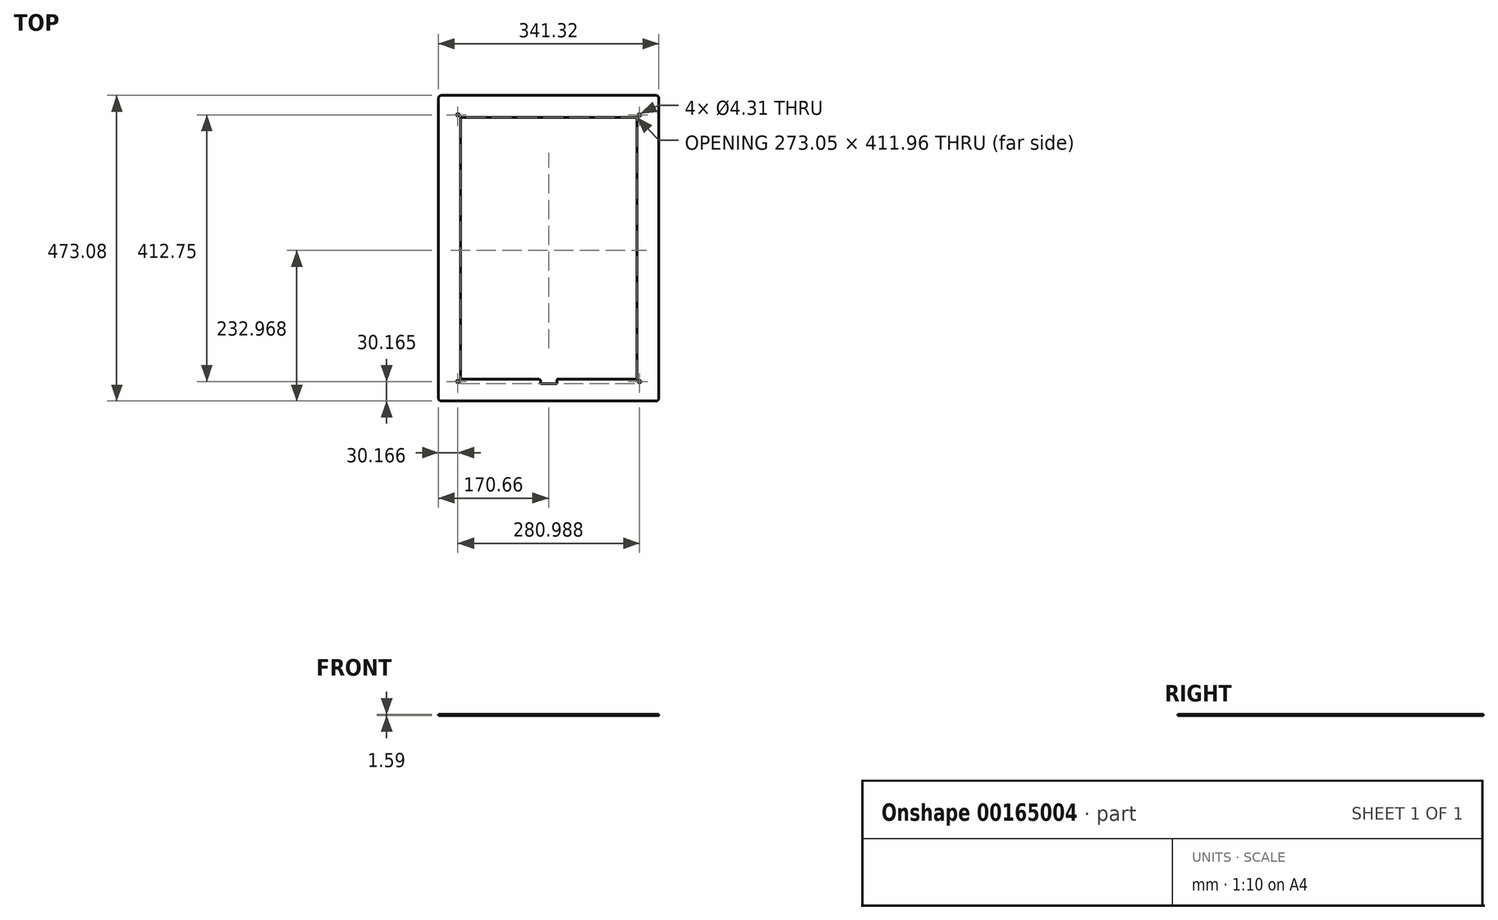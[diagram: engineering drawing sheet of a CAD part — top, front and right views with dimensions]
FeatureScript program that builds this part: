
annotation { "Feature Type Name" : "Feature", "Feature Type Description" : "" }
export const myFeature = defineFeature(function(context is Context, id is Id, definition is map)
    precondition{}
    {
        {
            var Q0;
            Q0=qCreatedBy(makeId("Top.planeOp"),FACE);
            var sketch = newSketch(context, id + "F0", { "sketchPlane" : qUnion([Q0])});
            skLineSegment(sketch, "E0.bottom", {"start": v(170.66, -236.54) * mm, "end": v(-170.66, -236.54) * mm});
            skLineSegment(sketch, "E0.top", {"start": v(170.66, 236.54) * mm, "end": v(-170.66, 236.54) * mm});
            skLineSegment(sketch, "E0.left", {"start": v(170.66, -236.54) * mm, "end": v(170.66, 236.54) * mm});
            skLineSegment(sketch, "E0.right", {"start": v(-170.66, -236.54) * mm, "end": v(-170.66, 236.54) * mm});
            skPoint(sketch, "E0.middle", {"position": v(0, 0) * mm});
            skLineSegment(sketch, "E1.bottom", {"start": v(140.5, 206.38) * mm, "end": v(-140.5, 206.38) * mm, "construction": true});
            skLineSegment(sketch, "E1.top", {"start": v(140.5, -206.38) * mm, "end": v(-140.5, -206.38) * mm, "construction": true});
            skLineSegment(sketch, "E1.left", {"start": v(140.5, 206.38) * mm, "end": v(140.5, -206.38) * mm, "construction": true});
            skLineSegment(sketch, "E1.right", {"start": v(-140.5, 206.38) * mm, "end": v(-140.5, -206.38) * mm, "construction": true});
            skLineSegment(sketch, "E2.bottom", {"start": v(136.53, 202.4) * mm, "end": v(-136.53, 202.4) * mm});
            skLineSegment(sketch, "E2.top", {"start": v(136.53, -202.4) * mm, "end": v(-136.53, -202.4) * mm});
            skLineSegment(sketch, "E2.left", {"start": v(136.53, 202.4) * mm, "end": v(136.53, -202.4) * mm});
            skLineSegment(sketch, "E2.right", {"start": v(-136.53, 202.4) * mm, "end": v(-136.53, -202.4) * mm});
            skLineSegment(sketch, "E3", {"start": v(136.53, 202.4) * mm, "end": v(136.53, 206.38) * mm, "construction": true});
            skLineSegment(sketch, "E4", {"start": v(136.53, 202.4) * mm, "end": v(140.5, 202.4) * mm, "construction": true});
            skLineSegment(sketch, "E5", {"start": v(140.5, 206.38) * mm, "end": v(140.5, 236.54) * mm, "construction": true});
            skLineSegment(sketch, "E6", {"start": v(140.5, 206.38) * mm, "end": v(170.66, 206.38) * mm, "construction": true});
            skCircle(sketch, "E7", {"center": v(-140.5, 206.38) * mm, "radius": 2.15 * mm});
            skCircle(sketch, "E8", {"center": v(140.5, 206.38) * mm, "radius": 2.15 * mm});
            skCircle(sketch, "E9", {"center": v(140.5, -206.38) * mm, "radius": 2.15 * mm});
            skCircle(sketch, "E10", {"center": v(-140.5, -206.38) * mm, "radius": 2.15 * mm});
            skSolve(sketch);
        }
        {
            var Q0;
            Q0 = qSketchRegion(id + "F0", true);
            extrude(context, id + "F1", {"entities" : qUnion([Q0]), "depth" : 1.59 * mm});
        }
        {
            var Q0;
            Q0=makeQuery(id+"F1.opExtrude","SWEPT_EDGE",EDGE,{"disambiguationData":[OSD([sQuery(id+"F0.wireOp",EDGE,"E0.top"),sQuery(id+"F0.wireOp",EDGE,"E0.right")])]});
            var Q1;
            Q1=makeQuery(id+"F1.opExtrude","SWEPT_EDGE",EDGE,{"disambiguationData":[OSD([sQuery(id+"F0.wireOp",EDGE,"E0.top"),sQuery(id+"F0.wireOp",EDGE,"E0.left")])]});
            var Q2;
            Q2=makeQuery(id+"F1.opExtrude","SWEPT_EDGE",EDGE,{"disambiguationData":[OSD([sQuery(id+"F0.wireOp",EDGE,"E0.bottom"),sQuery(id+"F0.wireOp",EDGE,"E0.left")])]});
            var Q3;
            Q3=makeQuery(id+"F1.opExtrude","SWEPT_EDGE",EDGE,{"disambiguationData":[OSD([sQuery(id+"F0.wireOp",EDGE,"E0.bottom"),sQuery(id+"F0.wireOp",EDGE,"E0.right")])]});
            fillet(context, id + "F2", {"entities" : qUnion([Q0, Q1, Q2, Q3]), "radius" : 4.76 * mm, "tangentPropagation" : true, "allowEdgeOverflow" : false});
        }
        {
            var Q0;
            Q0=makeQuery(id+"F1.opExtrude","CAP_FACE",FACE,{"disambiguationData":[OSD([sQuery(id+"F0.wireOp",EDGE,"E0.bottom"),sQuery(id+"F0.wireOp",EDGE,"E0.top"),sQuery(id+"F0.wireOp",EDGE,"E0.left"),sQuery(id+"F0.wireOp",EDGE,"E0.right"),sQuery(id+"F0.wireOp",EDGE,"E2.bottom"),sQuery(id+"F0.wireOp",EDGE,"E2.top"),sQuery(id+"F0.wireOp",EDGE,"E2.left"),sQuery(id+"F0.wireOp",EDGE,"E2.right"),sQuery(id+"F0.wireOp",EDGE,"E7"),sQuery(id+"F0.wireOp",EDGE,"E8"),sQuery(id+"F0.wireOp",EDGE,"E9"),sQuery(id+"F0.wireOp",EDGE,"E10")])],"isStart":false});
            var sketch = newSketch(context, id + "F3", { "sketchPlane" : qUnion([Q0])});
            skLineSegment(sketch, "E11", {"start": v(-140.5, -206.38) * mm, "end": v(-140.5, -211.14) * mm, "construction": true});
            skLineSegment(sketch, "E12", {"start": v(-140.5, -211.14) * mm, "end": v(0, -211.14) * mm, "construction": true});
            skLineSegment(sketch, "E13", {"start": v(0, -211.14) * mm, "end": v(0, -209.55) * mm, "construction": true});
            skLineSegment(sketch, "E14.bottom", {"start": v(-12.7, -202.4) * mm, "end": v(12.7, -202.4) * mm});
            skLineSegment(sketch, "E14.top", {"start": v(-12.7, -209.55) * mm, "end": v(12.7, -209.55) * mm});
            skLineSegment(sketch, "E14.left", {"start": v(-12.7, -202.4) * mm, "end": v(-12.7, -209.55) * mm});
            skLineSegment(sketch, "E14.right", {"start": v(12.7, -202.4) * mm, "end": v(12.7, -209.55) * mm});
            skLineSegment(sketch, "E15", {"start": v(0, -211.14) * mm, "end": v(0, -236.54) * mm, "construction": true});
            skSolve(sketch);
        }
        {
            var Q0;
            Q0 = qSketchRegion(id + "F3", true);
            var Q1;
            Q1=makeQuery(id+"F1.opExtrude","CAP_FACE",FACE,{"disambiguationData":[OSD([sQuery(id+"F0.wireOp",EDGE,"E0.bottom"),sQuery(id+"F0.wireOp",EDGE,"E0.top"),sQuery(id+"F0.wireOp",EDGE,"E0.left"),sQuery(id+"F0.wireOp",EDGE,"E0.right"),sQuery(id+"F0.wireOp",EDGE,"E2.bottom"),sQuery(id+"F0.wireOp",EDGE,"E2.top"),sQuery(id+"F0.wireOp",EDGE,"E2.left"),sQuery(id+"F0.wireOp",EDGE,"E2.right"),sQuery(id+"F0.wireOp",EDGE,"E7"),sQuery(id+"F0.wireOp",EDGE,"E8"),sQuery(id+"F0.wireOp",EDGE,"E9"),sQuery(id+"F0.wireOp",EDGE,"E10")])],"isStart":true});
            extrude(context, id + "F4", {"entities" : qUnion([Q0]), "operationType" : NewBodyOperationType.REMOVE, "endBound" : BoundingType.UP_TO_SURFACE, "oppositeDirection" : true, "endBoundEntityFace" : qUnion([Q1]), "depth" : 25.4 * mm});
        }
        {
            var Q0;
            Q0=makeQuery(id+"F4.boolean.opBoolean","COPY",EDGE,{"derivedFrom":makeQuery(id+"F4.opExtrude","SWEPT_EDGE",EDGE,{"disambiguationData":[OSD([sQuery(id+"F0.wireOp",EDGE,"E2.top"),sQuery(id+"F3.wireOp",EDGE,"E14.bottom"),sQuery(id+"F3.wireOp",EDGE,"E14.right")])]})});
            var Q1;
            Q1=makeQuery(id+"F4.boolean.opBoolean","COPY",EDGE,{"derivedFrom":makeQuery(id+"F4.opExtrude","SWEPT_EDGE",EDGE,{"disambiguationData":[OSD([sQuery(id+"F0.wireOp",EDGE,"E2.top"),sQuery(id+"F3.wireOp",EDGE,"E14.bottom"),sQuery(id+"F3.wireOp",EDGE,"E14.left")])]})});
            chamfer(context, id + "F5", {"entities" : qUnion([Q0, Q1]), "width" : 1.59 * mm, "tangentPropagation" : true});
        }
    });
